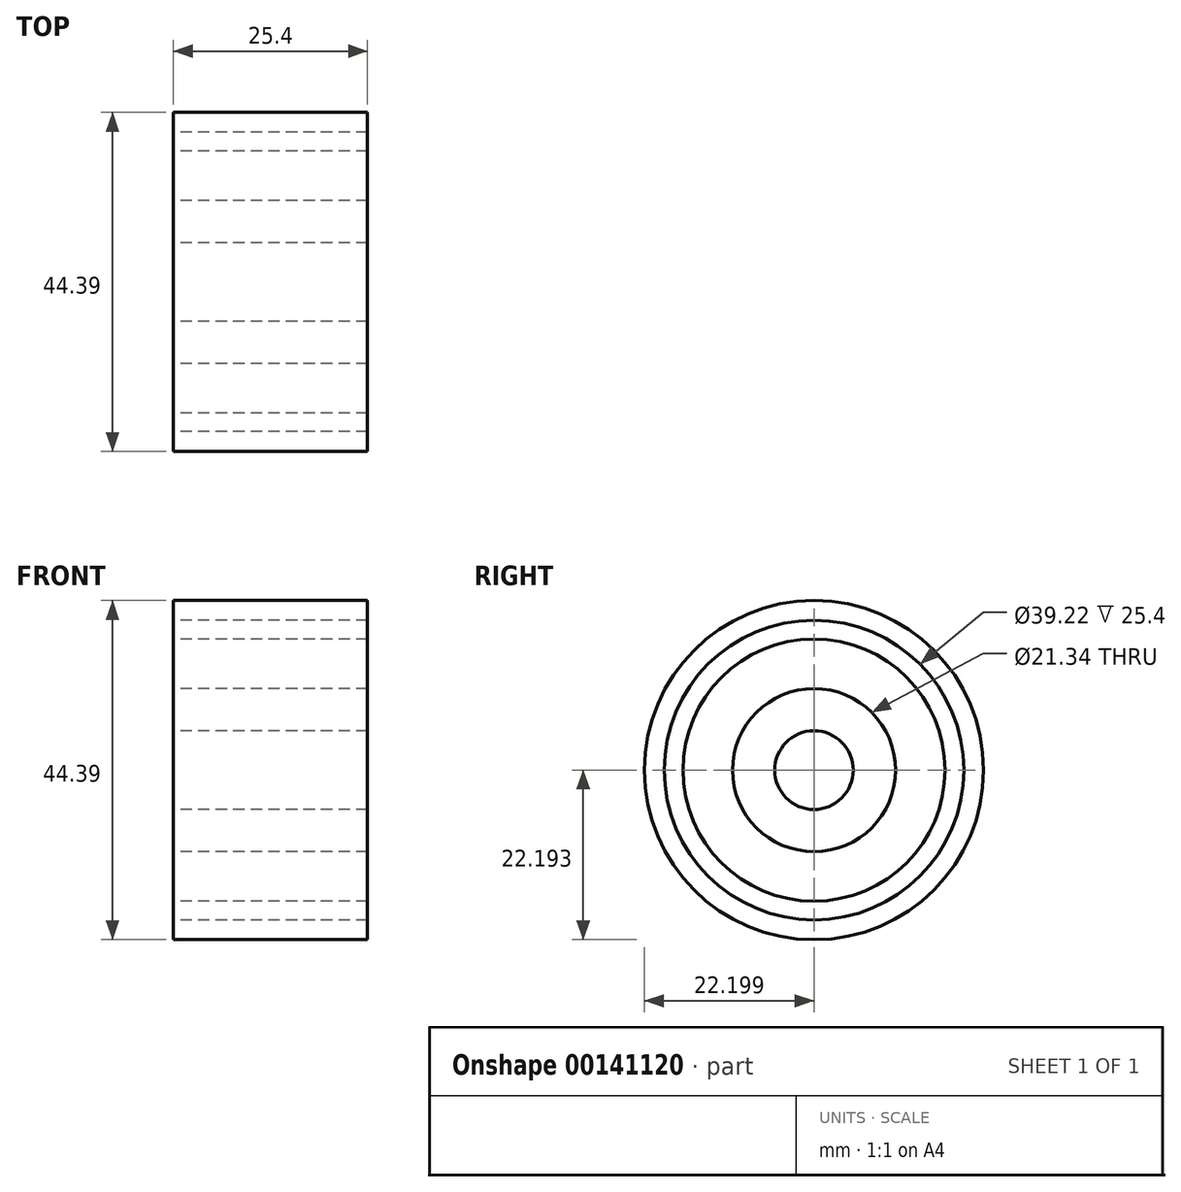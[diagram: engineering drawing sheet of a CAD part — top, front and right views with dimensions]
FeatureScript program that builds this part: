
annotation { "Feature Type Name" : "Feature", "Feature Type Description" : "" }
export const myFeature = defineFeature(function(context is Context, id is Id, definition is map)
    precondition{}
    {
        {
            var Q0;
            Q0=qCreatedBy(makeId("Right.planeOp"),FACE);
            var sketch = newSketch(context, id + "F0", { "sketchPlane" : qUnion([Q0])});
            skCircle(sketch, "E0", {"center": v(8.9, -38.7) * mm, "radius": 22.2 * mm});
            skCircle(sketch, "E1", {"center": v(8.9, -38.7) * mm, "radius": 19.61 * mm});
            skCircle(sketch, "E2", {"center": v(8.9, -38.7) * mm, "radius": 17.15 * mm});
            skCircle(sketch, "E3", {"center": v(8.9, -38.7) * mm, "radius": 14.35 * mm});
            skCircle(sketch, "E4", {"center": v(8.9, -38.7) * mm, "radius": 10.67 * mm});
            skCircle(sketch, "E5", {"center": v(8.9, -38.7) * mm, "radius": 7.78 * mm});
            skCircle(sketch, "E6", {"center": v(8.9, -38.7) * mm, "radius": 5.15 * mm});
            skSolve(sketch);
        }
        {
            var Q0;
            Q0 = qSketchRegion(id + "F0", true);
            var Q1;
            Q1=makeQuery(id+"F0.imprint","IMPRINT",FACE,{"disambiguationData":[TD([[makeQuery(id+"F0.imprint","IMPRINT",EDGE,{"derivedFrom":sQuery(id+"F0.wireOp",EDGE,"E6")}),1.0]])]});
            var Q2;
            Q2=makeQuery(id+"F0.imprint","IMPRINT",FACE,{"disambiguationData":[TD([[makeQuery(id+"F0.imprint","IMPRINT",EDGE,{"derivedFrom":sQuery(id+"F0.wireOp",EDGE,"E2")}),1.0]])]});
            var Q3;
            Q3=makeQuery(id+"F0.imprint","IMPRINT",FACE,{"disambiguationData":[TD([[makeQuery(id+"F0.imprint","IMPRINT",EDGE,{"derivedFrom":sQuery(id+"F0.wireOp",EDGE,"E3")}),1.0]])]});
            extrude(context, id + "F1", {"entities" : qUnion([Q0, Q1, Q2, Q3]), "depth" : 25.4 * mm});
        }
    });
